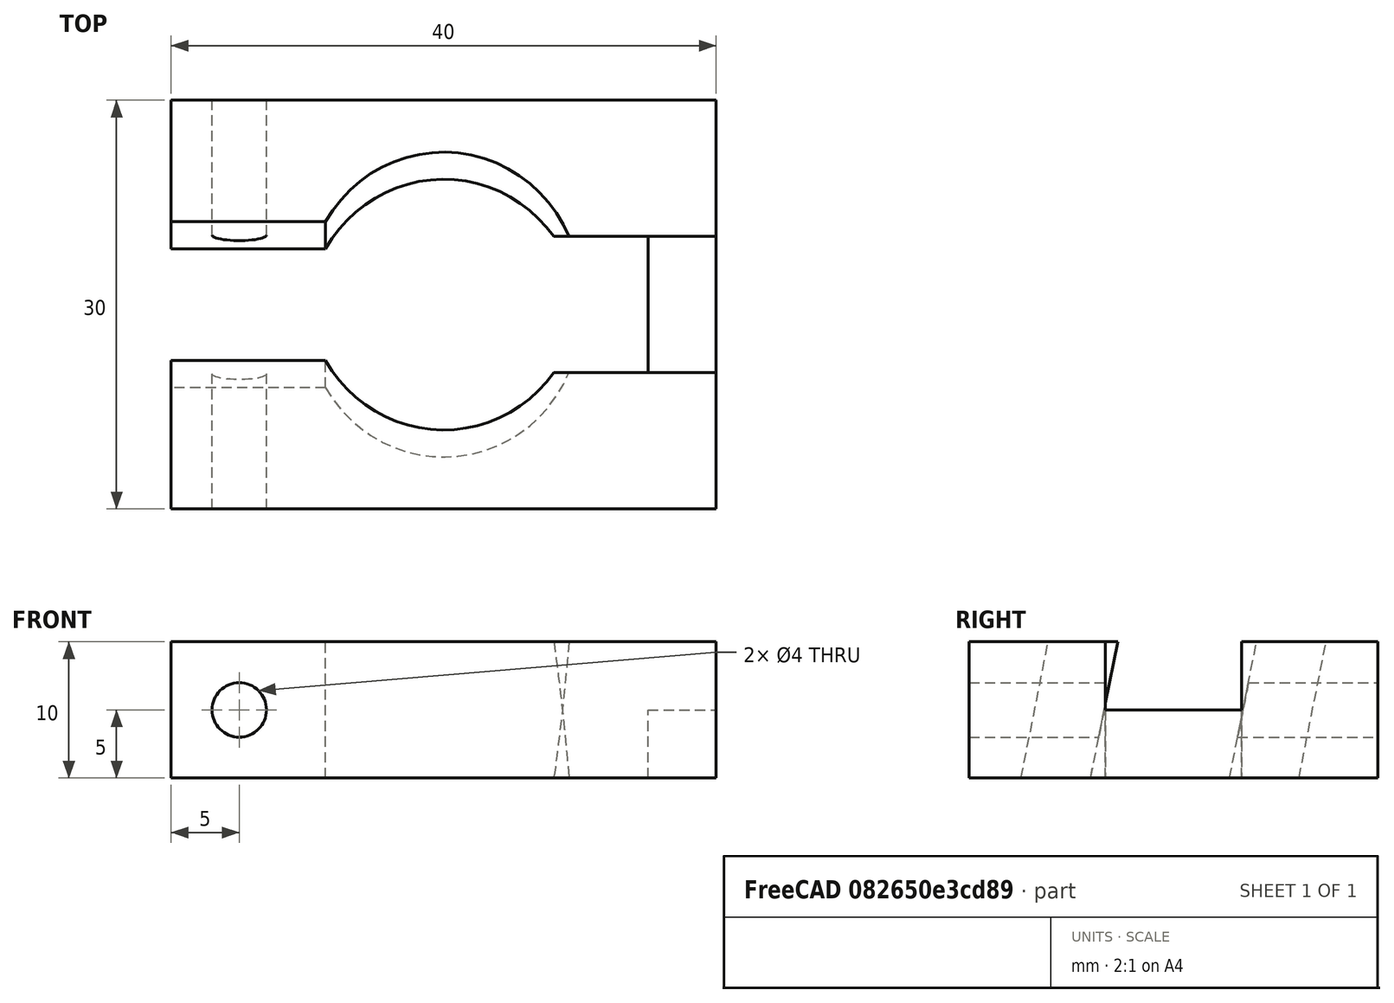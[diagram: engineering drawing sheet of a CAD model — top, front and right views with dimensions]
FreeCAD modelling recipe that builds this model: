
FCSTD DOCUMENT  (FreeCAD 0.17R13522 (Git))
Label: fastener-middleturn-20mm
License: All rights reserved
LicenseURL: http://en.wikipedia.org/wiki/All_rights_reserved
objects: Part::Box×4, Part::Cylinder×2, Part::MultiFuse×2, Part::Cut×1
note: 9 computed .brp shape members not serialized (recipe doc carries the construction recipe); baked Part::Feature solids carry a one-line shape summary decoded from their .brp

FEATURE [Part::Box] Box  label="Cube"
  AttacherType = Attacher::AttachEngine3D
  Height = 10
  Length = 40
  Placement = pos=(-20,-15,-5) rot=(0,0,1;0rad)
  Width = 30
FEATURE [Part::Box] Box001  label="Cube001"
  AttacherType = Attacher::AttachEngine3D
  Height = 10
  Length = 10
  Placement = pos=(5,-5,-5) rot=(0,0,1;0rad)
  Width = 10
FEATURE [Part::Box] Box002  label="Cube002"
  AttacherType = Attacher::AttachEngine3D
  Height = 5
  Length = 10
  Placement = pos=(10,-5,0) rot=(0,0,1;0rad)
  Width = 10
FEATURE [Part::Cylinder] Cylinder003
  Angle = 360
  AttacherType = Attacher::AttachEngine3D
  Height = 35
  Placement = pos=(-15,-15,0) rot=(-1,0,0;1.5708rad)
  Radius = 2
FEATURE [Part::Box] Box003  label="Squeeze Cube"
  AttacherType = Attacher::AttachEngine3D
  Height = 20
  Length = 15
  Placement = pos=(-20,-5,-10) rot=(0,0,1;0rad)
  Width = 10
FEATURE [Part::Cylinder] Cylinder004  label="Rail Cylinder"
  Angle = 360
  AttacherType = Attacher::AttachEngine3D
  Height = 20
  Placement = pos=(0,0,-10) rot=(0,0,1;0rad)
  Radius = 10
FEATURE [Part::MultiFuse] Fusion001
  Placement = pos=(0,0,0) rot=(-1,0,0;0.19635rad)
  Shapes = -> [Box003,Cylinder004]
FEATURE [Part::MultiFuse] Fusion  label="Negative Fusion"
  Shapes = -> [Box001,Box002,Cylinder003,Fusion001]
FEATURE [Part::Cut] Cut
  Base = -> Box
  Tool = -> Fusion
